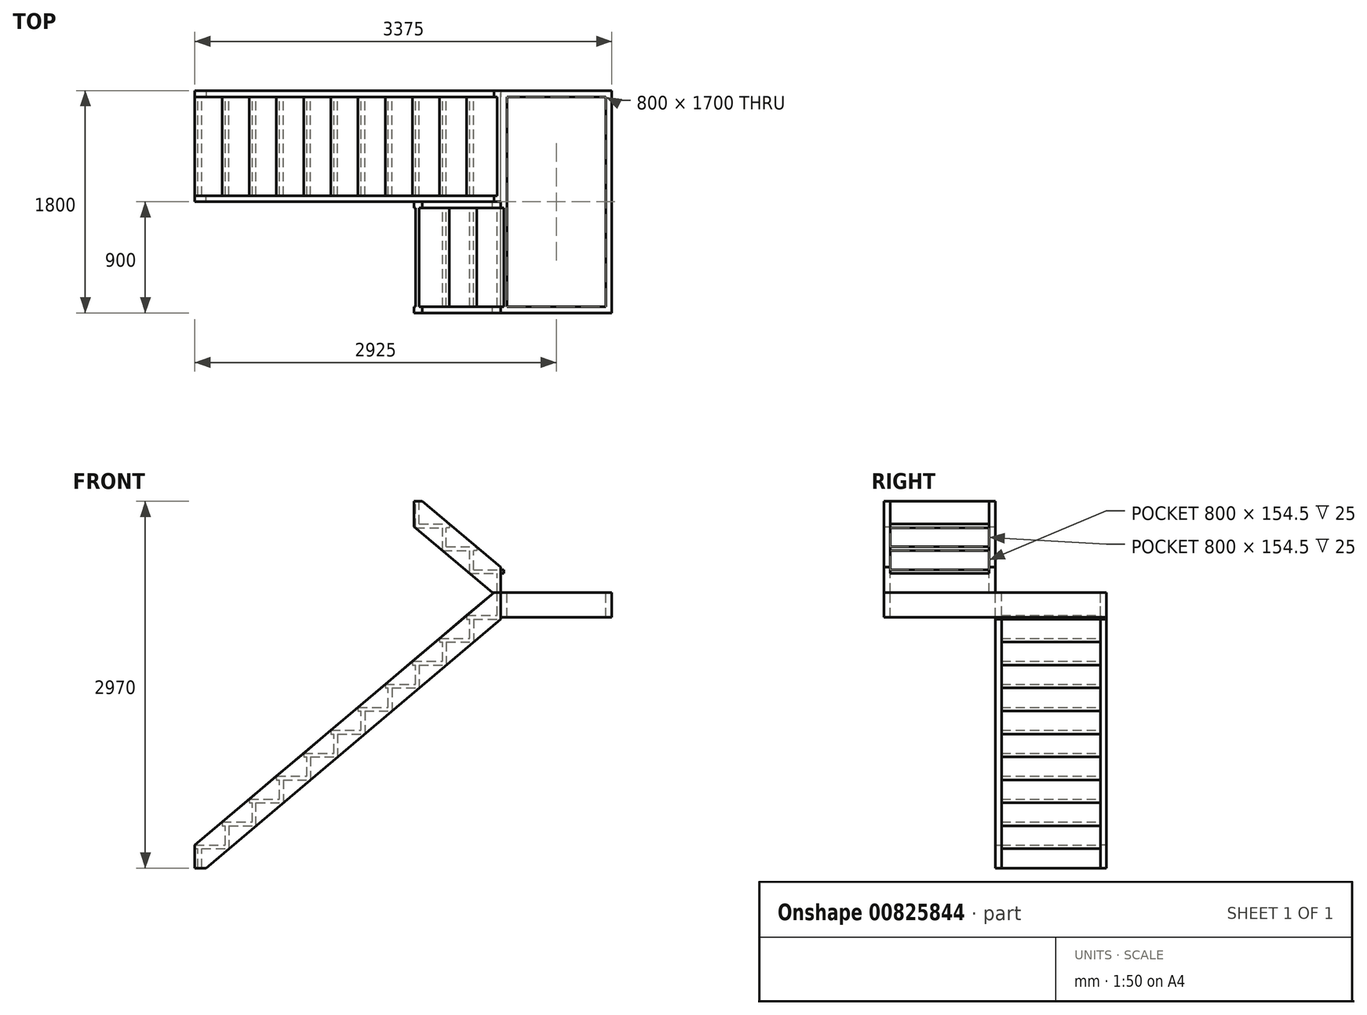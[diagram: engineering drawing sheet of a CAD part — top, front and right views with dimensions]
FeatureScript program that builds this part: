
annotation { "Feature Type Name" : "Feature", "Feature Type Description" : "" }
export const myFeature = defineFeature(function(context is Context, id is Id, definition is map)
    precondition{}
    {
        {
            var Q0;
            Q0=qCreatedBy(makeId("Front.planeOp"),FACE);
            var sketch = newSketch(context, id + "F0", { "sketchPlane" : qUnion([Q0])});
            skLineSegment(sketch, "E0", {"start": v(0, 0) * mm, "end": v(0, 156) * mm});
            skLineSegment(sketch, "E1", {"start": v(0, 186) * mm, "end": v(220, 186) * mm});
            skLineSegment(sketch, "E2", {"start": v(220, 186) * mm, "end": v(220, 342) * mm});
            skLineSegment(sketch, "E3", {"start": v(220, 372) * mm, "end": v(440, 372) * mm});
            skLineSegment(sketch, "E4", {"start": v(440, 372) * mm, "end": v(440, 528) * mm});
            skLineSegment(sketch, "E5", {"start": v(440, 558) * mm, "end": v(660, 558) * mm});
            skLineSegment(sketch, "E6", {"start": v(660, 558) * mm, "end": v(660, 714) * mm});
            skLineSegment(sketch, "E7", {"start": v(660, 744) * mm, "end": v(880, 744) * mm});
            skLineSegment(sketch, "E8", {"start": v(880, 744) * mm, "end": v(880, 900) * mm});
            skLineSegment(sketch, "E9", {"start": v(880, 930) * mm, "end": v(1100, 930) * mm});
            skLineSegment(sketch, "E10", {"start": v(1100, 930) * mm, "end": v(1100, 1086) * mm});
            skLineSegment(sketch, "E11", {"start": v(1100, 1116) * mm, "end": v(1320, 1116) * mm});
            skLineSegment(sketch, "E12", {"start": v(1320, 1116) * mm, "end": v(1320, 1272) * mm});
            skLineSegment(sketch, "E13", {"start": v(1320, 1302) * mm, "end": v(1540, 1302) * mm});
            skLineSegment(sketch, "E14", {"start": v(1540, 1302) * mm, "end": v(1540, 1458) * mm});
            skLineSegment(sketch, "E15", {"start": v(1540, 1488) * mm, "end": v(1760, 1488) * mm});
            skLineSegment(sketch, "E16", {"start": v(1760, 1488) * mm, "end": v(1760, 1644) * mm});
            skLineSegment(sketch, "E17", {"start": v(1760, 1674) * mm, "end": v(1980, 1674) * mm});
            skLineSegment(sketch, "E18", {"start": v(1980, 1674) * mm, "end": v(1980, 1830) * mm});
            skLineSegment(sketch, "E19", {"start": v(1980, 1860) * mm, "end": v(2200, 1860) * mm});
            skLineSegment(sketch, "E20", {"start": v(2200, 1860) * mm, "end": v(2200, 2016) * mm});
            skLineSegment(sketch, "E21", {"start": v(2200, 2046) * mm, "end": v(2420, 2046) * mm});
            skLineSegment(sketch, "E22", {"start": v(2420, 2046) * mm, "end": v(2420, 2232) * mm});
            skLineSegment(sketch, "E23.0", {"start": v(2230, 1860) * mm, "end": v(2230, 2016) * mm});
            skLineSegment(sketch, "E24.0", {"start": v(2200, 2016) * mm, "end": v(2420, 2016) * mm});
            skLineSegment(sketch, "E25.0", {"start": v(1980, 1830) * mm, "end": v(2200, 1830) * mm});
            skLineSegment(sketch, "E26.0", {"start": v(1760, 1644) * mm, "end": v(1980, 1644) * mm});
            skLineSegment(sketch, "E27.0", {"start": v(1790, 1488) * mm, "end": v(1790, 1644) * mm});
            skLineSegment(sketch, "E28.0", {"start": v(1540, 1458) * mm, "end": v(1760, 1458) * mm});
            skLineSegment(sketch, "E29.0", {"start": v(1570, 1302) * mm, "end": v(1570, 1458) * mm});
            skLineSegment(sketch, "E30.0", {"start": v(1320, 1272) * mm, "end": v(1540, 1272) * mm});
            skLineSegment(sketch, "E31.0", {"start": v(1350, 1116) * mm, "end": v(1350, 1272) * mm});
            skLineSegment(sketch, "E32.0", {"start": v(1100, 1086) * mm, "end": v(1320, 1086) * mm});
            skLineSegment(sketch, "E33.0", {"start": v(1130, 930) * mm, "end": v(1130, 1086) * mm});
            skLineSegment(sketch, "E34.0", {"start": v(880, 900) * mm, "end": v(1100, 900) * mm});
            skLineSegment(sketch, "E35.0", {"start": v(910, 744) * mm, "end": v(910, 900) * mm});
            skLineSegment(sketch, "E36.0", {"start": v(660, 714) * mm, "end": v(880, 714) * mm});
            skLineSegment(sketch, "E37.0", {"start": v(690, 558) * mm, "end": v(690, 714) * mm});
            skLineSegment(sketch, "E38.0", {"start": v(440, 528) * mm, "end": v(660, 528) * mm});
            skLineSegment(sketch, "E39.0", {"start": v(470, 372) * mm, "end": v(470, 528) * mm});
            skLineSegment(sketch, "E40.0", {"start": v(220, 342) * mm, "end": v(440, 342) * mm});
            skLineSegment(sketch, "E41.0", {"start": v(250, 186) * mm, "end": v(250, 342) * mm});
            skLineSegment(sketch, "E42.0", {"start": v(0, 156) * mm, "end": v(220, 156) * mm});
            skLineSegment(sketch, "E43.0", {"start": v(30, 0) * mm, "end": v(30, 156) * mm});
            skLineSegment(sketch, "E44", {"start": v(0, 0) * mm, "end": v(30, 0) * mm});
            skLineSegment(sketch, "E45", {"start": v(220, 156) * mm, "end": v(250, 156) * mm});
            skLineSegment(sketch, "E46", {"start": v(250, 186) * mm, "end": v(250, 156) * mm});
            skLineSegment(sketch, "E47", {"start": v(440, 342) * mm, "end": v(470, 342) * mm});
            skLineSegment(sketch, "E48", {"start": v(690, 558) * mm, "end": v(690, 528) * mm});
            skLineSegment(sketch, "E49", {"start": v(690, 528) * mm, "end": v(660, 528) * mm});
            skLineSegment(sketch, "E50", {"start": v(910, 744) * mm, "end": v(910, 714) * mm});
            skLineSegment(sketch, "E51", {"start": v(910, 714) * mm, "end": v(880, 714) * mm});
            skLineSegment(sketch, "E52", {"start": v(1130, 930) * mm, "end": v(1130, 900) * mm});
            skLineSegment(sketch, "E53", {"start": v(1130, 900) * mm, "end": v(1100, 900) * mm});
            skLineSegment(sketch, "E54", {"start": v(1350, 1116) * mm, "end": v(1350, 1086) * mm});
            skLineSegment(sketch, "E55", {"start": v(1350, 1086) * mm, "end": v(1320, 1086) * mm});
            skLineSegment(sketch, "E56", {"start": v(1570, 1302) * mm, "end": v(1570, 1272) * mm});
            skLineSegment(sketch, "E57", {"start": v(1570, 1272) * mm, "end": v(1540, 1272) * mm});
            skLineSegment(sketch, "E58", {"start": v(1790, 1488) * mm, "end": v(1790, 1458) * mm});
            skLineSegment(sketch, "E59", {"start": v(1790, 1458) * mm, "end": v(1760, 1458) * mm});
            skLineSegment(sketch, "E60", {"start": v(2010, 1674) * mm, "end": v(2010, 1644) * mm});
            skLineSegment(sketch, "E61", {"start": v(2010, 1644) * mm, "end": v(1980, 1644) * mm});
            skLineSegment(sketch, "E62", {"start": v(2230, 1860) * mm, "end": v(2230, 1830) * mm});
            skLineSegment(sketch, "E63", {"start": v(2230, 1830) * mm, "end": v(2200, 1830) * mm});
            skLineSegment(sketch, "E64", {"start": v(2200, 2046) * mm, "end": v(2175, 2046) * mm});
            skLineSegment(sketch, "E65", {"start": v(2175, 2046) * mm, "end": v(2175, 2016) * mm});
            skLineSegment(sketch, "E66", {"start": v(2175, 2016) * mm, "end": v(2200, 2016) * mm});
            skLineSegment(sketch, "E67", {"start": v(1980, 1860) * mm, "end": v(1955, 1860) * mm});
            skLineSegment(sketch, "E68", {"start": v(1955, 1860) * mm, "end": v(1955, 1830) * mm});
            skLineSegment(sketch, "E69", {"start": v(1955, 1830) * mm, "end": v(1980, 1830) * mm});
            skLineSegment(sketch, "E70", {"start": v(1760, 1674) * mm, "end": v(1735, 1674) * mm});
            skLineSegment(sketch, "E71", {"start": v(1735, 1674) * mm, "end": v(1735, 1644) * mm});
            skLineSegment(sketch, "E72", {"start": v(1735, 1644) * mm, "end": v(1760, 1644) * mm});
            skLineSegment(sketch, "E73", {"start": v(1540, 1488) * mm, "end": v(1515, 1488) * mm});
            skLineSegment(sketch, "E74", {"start": v(1515, 1488) * mm, "end": v(1515, 1458) * mm});
            skLineSegment(sketch, "E75", {"start": v(1515, 1458) * mm, "end": v(1540, 1458) * mm});
            skLineSegment(sketch, "E76", {"start": v(1320, 1302) * mm, "end": v(1295, 1302) * mm});
            skLineSegment(sketch, "E77", {"start": v(1295, 1302) * mm, "end": v(1295, 1272) * mm});
            skLineSegment(sketch, "E78", {"start": v(1295, 1272) * mm, "end": v(1320, 1272) * mm});
            skLineSegment(sketch, "E79", {"start": v(1100, 1116) * mm, "end": v(1075, 1116) * mm});
            skLineSegment(sketch, "E80", {"start": v(1075, 1116) * mm, "end": v(1075, 1086) * mm});
            skLineSegment(sketch, "E81", {"start": v(1075, 1086) * mm, "end": v(1100, 1086) * mm});
            skLineSegment(sketch, "E82", {"start": v(880, 930) * mm, "end": v(855, 930) * mm});
            skLineSegment(sketch, "E83", {"start": v(855, 930) * mm, "end": v(855, 900) * mm});
            skLineSegment(sketch, "E84", {"start": v(855, 900) * mm, "end": v(880, 900) * mm});
            skLineSegment(sketch, "E85", {"start": v(660, 744) * mm, "end": v(635, 744) * mm});
            skLineSegment(sketch, "E86", {"start": v(635, 744) * mm, "end": v(635, 714) * mm});
            skLineSegment(sketch, "E87", {"start": v(635, 714) * mm, "end": v(660, 714) * mm});
            skLineSegment(sketch, "E88", {"start": v(440, 558) * mm, "end": v(415, 558) * mm});
            skLineSegment(sketch, "E89", {"start": v(415, 558) * mm, "end": v(415, 528) * mm});
            skLineSegment(sketch, "E90", {"start": v(415, 528) * mm, "end": v(440, 528) * mm});
            skLineSegment(sketch, "E91", {"start": v(220, 372) * mm, "end": v(195, 372) * mm});
            skLineSegment(sketch, "E92", {"start": v(195, 372) * mm, "end": v(195, 342) * mm});
            skLineSegment(sketch, "E93", {"start": v(0, 186) * mm, "end": v(-25, 186) * mm});
            skLineSegment(sketch, "E94", {"start": v(-25, 186) * mm, "end": v(-25, 156) * mm});
            skLineSegment(sketch, "E95", {"start": v(-25, 156) * mm, "end": v(0, 156) * mm});
            skLineSegment(sketch, "E96", {"start": v(195, 342) * mm, "end": v(220, 342) * mm});
            skLineSegment(sketch, "E97", {"start": v(470, 342) * mm, "end": v(470, 372) * mm});
            skLineSegment(sketch, "E98", {"start": v(2010, 1674) * mm, "end": v(2010, 1830) * mm});
            skLineSegment(sketch, "E99.0", {"start": v(2450, 2016) * mm, "end": v(2450, 2232) * mm});
            skLineSegment(sketch, "E100", {"start": v(2420, 2016) * mm, "end": v(2450, 2016) * mm});
            skLineSegment(sketch, "E101", {"start": v(2420, 2232) * mm, "end": v(2450, 2232) * mm});
            skLineSegment(sketch, "E102", {"start": v(2420, 2046) * mm, "end": v(2450, 2046) * mm});
            skLineSegment(sketch, "E103", {"start": v(2200, 1860) * mm, "end": v(2230, 1860) * mm});
            skLineSegment(sketch, "E104", {"start": v(1980, 1674) * mm, "end": v(2010, 1674) * mm});
            skLineSegment(sketch, "E105", {"start": v(1760, 1488) * mm, "end": v(1790, 1488) * mm});
            skLineSegment(sketch, "E106", {"start": v(1540, 1302) * mm, "end": v(1570, 1302) * mm});
            skLineSegment(sketch, "E107", {"start": v(1320, 1116) * mm, "end": v(1350, 1116) * mm});
            skLineSegment(sketch, "E108", {"start": v(1100, 930) * mm, "end": v(1130, 930) * mm});
            skLineSegment(sketch, "E109", {"start": v(880, 744) * mm, "end": v(910, 744) * mm});
            skLineSegment(sketch, "E110", {"start": v(660, 558) * mm, "end": v(690, 558) * mm});
            skLineSegment(sketch, "E111", {"start": v(440, 372) * mm, "end": v(470, 372) * mm});
            skLineSegment(sketch, "E112", {"start": v(220, 186) * mm, "end": v(250, 186) * mm});
            skSolve(sketch);
        }
        {
            var Q0;
            Q0=qCreatedBy(makeId("Front.planeOp"),FACE);
            var sketch = newSketch(context, id + "F1", { "sketchPlane" : qUnion([Q0])});
            skLineSegment(sketch, "E113", {"start": v(2420, 2232) * mm, "end": v(2420, 2416.5) * mm});
            skLineSegment(sketch, "E114", {"start": v(2420, 2416.5) * mm, "end": v(2200, 2416.5) * mm});
            skLineSegment(sketch, "E115", {"start": v(2200, 2416.5) * mm, "end": v(2200, 2601) * mm});
            skLineSegment(sketch, "E116", {"start": v(2200, 2601) * mm, "end": v(1980, 2601) * mm});
            skLineSegment(sketch, "E117", {"start": v(1980, 2601) * mm, "end": v(1980, 2785.5) * mm});
            skLineSegment(sketch, "E118", {"start": v(1980, 2785.5) * mm, "end": v(1760, 2785.5) * mm});
            skLineSegment(sketch, "E119", {"start": v(1760, 2785.5) * mm, "end": v(1760, 2970) * mm});
            skPoint(sketch, "E120.end.orphan", {"position": v(1760, 2970) * mm});
            skSolve(sketch);
        }
        {
            var Q0;
            Q0=qCreatedBy(makeId("Front.planeOp"),FACE);
            var sketch = newSketch(context, id + "F2", { "sketchPlane" : qUnion([Q0])});
            skLineSegment(sketch, "E121", {"start": v(0, 0) * mm, "end": v(4057.25, 0) * mm, "construction": true});
            skLineSegment(sketch, "E122.0", {"start": v(0, 2775) * mm, "end": v(4057.25, 2775) * mm, "construction": true});
            skLineSegment(sketch, "E123.0", {"start": v(0, 775) * mm, "end": v(4057.25, 775) * mm, "construction": true});
            skLineSegment(sketch, "E124", {"start": v(660, 714) * mm, "end": v(660, 3042.77) * mm, "construction": true});
            skSolve(sketch);
        }
        {
            var Q0;
            Q0 = qSketchRegion(id + "F0", true);
            extrude(context, id + "F3", {"entities" : qUnion([Q0]), "depth" : 800 * mm, "offsetDistance" : 25 * mm});
        }
        {
            var Q0;
            Q0=qCreatedBy(makeId("Front.planeOp"),FACE);
            var sketch = newSketch(context, id + "F4", { "sketchPlane" : qUnion([Q0])});
            skLineSegment(sketch, "E125", {"start": v(-25, 186) * mm, "end": v(2395, 2232) * mm});
            skLineSegment(sketch, "E126", {"start": v(65.48, 0) * mm, "end": v(2450, 2016) * mm});
            skLineSegment(sketch, "E127", {"start": v(2395, 2232) * mm, "end": v(2450, 2232) * mm});
            skLineSegment(sketch, "E128", {"start": v(2450, 2232) * mm, "end": v(2450, 2016) * mm});
            skLineSegment(sketch, "E129", {"start": v(-25, 186) * mm, "end": v(-25, 0) * mm});
            skLineSegment(sketch, "E130", {"start": v(-25, 0) * mm, "end": v(65.48, 0) * mm});
            skSolve(sketch);
        }
        {
            var Q0;
            Q0 = qSketchRegion(id + "F0", true);
            extrude(context, id + "F5", {"entities" : qUnion([Q0]), "operationType" : NewBodyOperationType.ADD, "depth" : 800 * mm, "offsetDistance" : 25 * mm});
        }
        {
            var Q0;
            Q0 = qSketchRegion(id + "F4", true);
            extrude(context, id + "F6", {"entities" : qUnion([Q0]), "operationType" : NewBodyOperationType.ADD, "oppositeDirection" : true, "depth" : 50 * mm, "offsetDistance" : 25 * mm});
        }
        {
            var Q0;
            Q0=makeQuery(id+"F3.opExtrude","CAP_FACE",FACE,{"disambiguationData":[OSD([sQuery(id+"F0.wireOp",EDGE,"E0"),sQuery(id+"F0.wireOp",EDGE,"E1"),sQuery(id+"F0.wireOp",EDGE,"E2"),sQuery(id+"F0.wireOp",EDGE,"E3"),sQuery(id+"F0.wireOp",EDGE,"E4"),sQuery(id+"F0.wireOp",EDGE,"E5"),sQuery(id+"F0.wireOp",EDGE,"E6"),sQuery(id+"F0.wireOp",EDGE,"E7"),sQuery(id+"F0.wireOp",EDGE,"E8"),sQuery(id+"F0.wireOp",EDGE,"E9"),sQuery(id+"F0.wireOp",EDGE,"E10"),sQuery(id+"F0.wireOp",EDGE,"E11"),sQuery(id+"F0.wireOp",EDGE,"E12"),sQuery(id+"F0.wireOp",EDGE,"E13"),sQuery(id+"F0.wireOp",EDGE,"E14"),sQuery(id+"F0.wireOp",EDGE,"E15"),sQuery(id+"F0.wireOp",EDGE,"E16"),sQuery(id+"F0.wireOp",EDGE,"E17"),sQuery(id+"F0.wireOp",EDGE,"E18"),sQuery(id+"F0.wireOp",EDGE,"E19"),sQuery(id+"F0.wireOp",EDGE,"E20"),sQuery(id+"F0.wireOp",EDGE,"E21"),sQuery(id+"F0.wireOp",EDGE,"E22"),sQuery(id+"F0.wireOp",EDGE,"E23.0"),sQuery(id+"F0.wireOp",EDGE,"E24.0"),sQuery(id+"F0.wireOp",EDGE,"E25.0"),sQuery(id+"F0.wireOp",EDGE,"E26.0"),sQuery(id+"F0.wireOp",EDGE,"E27.0"),sQuery(id+"F0.wireOp",EDGE,"E28.0"),sQuery(id+"F0.wireOp",EDGE,"E29.0"),sQuery(id+"F0.wireOp",EDGE,"E30.0"),sQuery(id+"F0.wireOp",EDGE,"E31.0"),sQuery(id+"F0.wireOp",EDGE,"E32.0"),sQuery(id+"F0.wireOp",EDGE,"E33.0"),sQuery(id+"F0.wireOp",EDGE,"E34.0"),sQuery(id+"F0.wireOp",EDGE,"E35.0"),sQuery(id+"F0.wireOp",EDGE,"E36.0"),sQuery(id+"F0.wireOp",EDGE,"E37.0"),sQuery(id+"F0.wireOp",EDGE,"E38.0"),sQuery(id+"F0.wireOp",EDGE,"E39.0"),sQuery(id+"F0.wireOp",EDGE,"E40.0"),sQuery(id+"F0.wireOp",EDGE,"E41.0"),sQuery(id+"F0.wireOp",EDGE,"E42.0"),sQuery(id+"F0.wireOp",EDGE,"E43.0"),sQuery(id+"F0.wireOp",EDGE,"E44"),sQuery(id+"F0.wireOp",EDGE,"E45"),sQuery(id+"F0.wireOp",EDGE,"E46"),sQuery(id+"F0.wireOp",EDGE,"E47"),sQuery(id+"F0.wireOp",EDGE,"E48"),sQuery(id+"F0.wireOp",EDGE,"E49"),sQuery(id+"F0.wireOp",EDGE,"E50"),sQuery(id+"F0.wireOp",EDGE,"E51"),sQuery(id+"F0.wireOp",EDGE,"E52"),sQuery(id+"F0.wireOp",EDGE,"E53"),sQuery(id+"F0.wireOp",EDGE,"E54"),sQuery(id+"F0.wireOp",EDGE,"E55"),sQuery(id+"F0.wireOp",EDGE,"E56"),sQuery(id+"F0.wireOp",EDGE,"E57"),sQuery(id+"F0.wireOp",EDGE,"E58"),sQuery(id+"F0.wireOp",EDGE,"E59"),sQuery(id+"F0.wireOp",EDGE,"E60"),sQuery(id+"F0.wireOp",EDGE,"E61"),sQuery(id+"F0.wireOp",EDGE,"E62"),sQuery(id+"F0.wireOp",EDGE,"E63"),sQuery(id+"F0.wireOp",EDGE,"E64"),sQuery(id+"F0.wireOp",EDGE,"E65"),sQuery(id+"F0.wireOp",EDGE,"E66"),sQuery(id+"F0.wireOp",EDGE,"E67"),sQuery(id+"F0.wireOp",EDGE,"E68"),sQuery(id+"F0.wireOp",EDGE,"E69"),sQuery(id+"F0.wireOp",EDGE,"E70"),sQuery(id+"F0.wireOp",EDGE,"E71"),sQuery(id+"F0.wireOp",EDGE,"E72"),sQuery(id+"F0.wireOp",EDGE,"E73"),sQuery(id+"F0.wireOp",EDGE,"E74"),sQuery(id+"F0.wireOp",EDGE,"E75"),sQuery(id+"F0.wireOp",EDGE,"E76"),sQuery(id+"F0.wireOp",EDGE,"E77"),sQuery(id+"F0.wireOp",EDGE,"E78"),sQuery(id+"F0.wireOp",EDGE,"E79"),sQuery(id+"F0.wireOp",EDGE,"E80"),sQuery(id+"F0.wireOp",EDGE,"E81"),sQuery(id+"F0.wireOp",EDGE,"E82"),sQuery(id+"F0.wireOp",EDGE,"E83"),sQuery(id+"F0.wireOp",EDGE,"E84"),sQuery(id+"F0.wireOp",EDGE,"E85"),sQuery(id+"F0.wireOp",EDGE,"E86"),sQuery(id+"F0.wireOp",EDGE,"E87"),sQuery(id+"F0.wireOp",EDGE,"E88"),sQuery(id+"F0.wireOp",EDGE,"E89"),sQuery(id+"F0.wireOp",EDGE,"E90"),sQuery(id+"F0.wireOp",EDGE,"E91"),sQuery(id+"F0.wireOp",EDGE,"E92"),sQuery(id+"F0.wireOp",EDGE,"E93"),sQuery(id+"F0.wireOp",EDGE,"E94"),sQuery(id+"F0.wireOp",EDGE,"E95"),sQuery(id+"F0.wireOp",EDGE,"E96"),sQuery(id+"F0.wireOp",EDGE,"E97"),sQuery(id+"F0.wireOp",EDGE,"E98"),sQuery(id+"F0.wireOp",EDGE,"E99.0"),sQuery(id+"F0.wireOp",EDGE,"E100"),sQuery(id+"F0.wireOp",EDGE,"E101")])],"isStart":false});
            var sketch = newSketch(context, id + "F7", { "sketchPlane" : qUnion([Q0])});
            skLineSegment(sketch, "E131", {"start": v(2450, 2016) * mm, "end": v(2450, 2232) * mm});
            skLineSegment(sketch, "E132", {"start": v(2450, 2232) * mm, "end": v(2396.45, 2232) * mm});
            skLineSegment(sketch, "E133", {"start": v(2396.45, 2232) * mm, "end": v(-25, 186) * mm});
            skLineSegment(sketch, "E134", {"start": v(-25, 186) * mm, "end": v(-25, 0) * mm});
            skLineSegment(sketch, "E135", {"start": v(-25, 0) * mm, "end": v(65.48, 0) * mm});
            skLineSegment(sketch, "E136", {"start": v(65.48, 0) * mm, "end": v(2450, 2016) * mm});
            skSolve(sketch);
        }
        {
            var Q0;
            Q0 = qSketchRegion(id + "F7", true);
            extrude(context, id + "F8", {"entities" : qUnion([Q0]), "operationType" : NewBodyOperationType.ADD, "depth" : 50 * mm, "offsetDistance" : 25 * mm});
        }
        {
            var Q0;
            Q0=makeQuery(id+"F8.boolean.opBoolean","MERGE",FACE,{"derivedFrom":[makeQuery(id+"F6.boolean.opBoolean","MERGE",FACE,{"derivedFrom":[makeQuery(id+"F3.opExtrude","SWEPT_FACE",FACE,{"disambiguationData":[OSD([sQuery(id+"F0.wireOp",EDGE,"E101")])]}),makeQuery(id+"F6.opExtrude","SWEPT_FACE",FACE,{"disambiguationData":[OSD([sQuery(id+"F4.wireOp",EDGE,"E127")])]})]}),makeQuery(id+"F8.opExtrude","SWEPT_FACE",FACE,{"disambiguationData":[OSD([sQuery(id+"F7.wireOp",EDGE,"E132")])]})]});
            var sketch = newSketch(context, id + "F9", { "sketchPlane" : qUnion([Q0])});
            skLineSegment(sketch, "E137", {"start": v(2450, 50) * mm, "end": v(2450, -1750) * mm});
            skLineSegment(sketch, "E138", {"start": v(2450, -1750) * mm, "end": v(3350, -1750) * mm});
            skLineSegment(sketch, "E139", {"start": v(3350, -1750) * mm, "end": v(3350, 50) * mm});
            skLineSegment(sketch, "E140", {"start": v(3350, 50) * mm, "end": v(2450, 50) * mm});
            skLineSegment(sketch, "E141.0", {"start": v(3300, -1700) * mm, "end": v(3300, 0) * mm});
            skLineSegment(sketch, "E142.0", {"start": v(3300, 0) * mm, "end": v(2500, 0) * mm});
            skLineSegment(sketch, "E143.0", {"start": v(2500, 0) * mm, "end": v(2500, -1700) * mm});
            skLineSegment(sketch, "E144.0", {"start": v(2500, -1700) * mm, "end": v(3300, -1700) * mm});
            skSolve(sketch);
        }
        {
            var Q0;
            Q0 = qSketchRegion(id + "F9", true);
            extrude(context, id + "F10", {"entities" : qUnion([Q0]), "operationType" : NewBodyOperationType.ADD, "oppositeDirection" : true, "depth" : 200 * mm, "offsetDistance" : 25 * mm});
        }
        {
            var Q0;
            Q0=makeQuery(id+"F8.opExtrude","CAP_FACE",FACE,{"disambiguationData":[OSD([sQuery(id+"F7.wireOp",EDGE,"E131"),sQuery(id+"F7.wireOp",EDGE,"E132"),sQuery(id+"F7.wireOp",EDGE,"E133"),sQuery(id+"F7.wireOp",EDGE,"E134"),sQuery(id+"F7.wireOp",EDGE,"E135"),sQuery(id+"F7.wireOp",EDGE,"E136")])],"isStart":false});
            var sketch = newSketch(context, id + "F11", { "sketchPlane" : qUnion([Q0])});
            skLineSegment(sketch, "E145", {"start": v(2450, 2232) * mm, "end": v(2450, 2416.5) * mm, "construction": true});
            skLineSegment(sketch, "E146", {"start": v(2450, 2416.5) * mm, "end": v(2230, 2416.5) * mm, "construction": true});
            skLineSegment(sketch, "E147", {"start": v(2230, 2416.5) * mm, "end": v(2230, 2601) * mm, "construction": true});
            skLineSegment(sketch, "E148", {"start": v(2230, 2601) * mm, "end": v(2010, 2601) * mm, "construction": true});
            skLineSegment(sketch, "E149", {"start": v(2010, 2601) * mm, "end": v(2010, 2785.5) * mm, "construction": true});
            skLineSegment(sketch, "E150", {"start": v(2010, 2785.5) * mm, "end": v(1790, 2785.5) * mm, "construction": true});
            skLineSegment(sketch, "E151", {"start": v(1790, 2785.5) * mm, "end": v(1790, 2970) * mm, "construction": true});
            skLineSegment(sketch, "E152.0", {"start": v(1760, 2970) * mm, "end": v(1760, 2971.67) * mm, "construction": true});
            skLineSegment(sketch, "E153.0", {"start": v(2010, 2755.5) * mm, "end": v(1790, 2755.5) * mm, "construction": true});
            skLineSegment(sketch, "E154.0", {"start": v(1980, 2601) * mm, "end": v(1980, 2785.5) * mm, "construction": true});
            skLineSegment(sketch, "E155.0", {"start": v(2230, 2571) * mm, "end": v(2010, 2571) * mm, "construction": true});
            skLineSegment(sketch, "E156.0", {"start": v(2200, 2416.5) * mm, "end": v(2200, 2601) * mm, "construction": true});
            skLineSegment(sketch, "E157.0", {"start": v(2450, 2386.5) * mm, "end": v(2230, 2386.5) * mm, "construction": true});
            skLineSegment(sketch, "E158", {"start": v(2200, 2416.5) * mm, "end": v(2200, 2386.5) * mm, "construction": true});
            skLineSegment(sketch, "E159", {"start": v(2200, 2386.5) * mm, "end": v(2230, 2386.5) * mm, "construction": true});
            skLineSegment(sketch, "E160", {"start": v(2010, 2571) * mm, "end": v(1980, 2571) * mm, "construction": true});
            skLineSegment(sketch, "E161", {"start": v(1980, 2571) * mm, "end": v(1980, 2601) * mm, "construction": true});
            skLineSegment(sketch, "E162", {"start": v(1790, 2755.5) * mm, "end": v(1760, 2755.5) * mm, "construction": true});
            skLineSegment(sketch, "E163.0", {"start": v(2420, 2232) * mm, "end": v(2420, 2416.5) * mm});
            skLineSegment(sketch, "E164", {"start": v(2450, 2232) * mm, "end": v(2450, 2416.5) * mm});
            skLineSegment(sketch, "E165", {"start": v(1760, 2971.67) * mm, "end": v(1760, 2970) * mm});
            skLineSegment(sketch, "E166.0", {"start": v(2170, 2416.5) * mm, "end": v(2170, 2386.5) * mm});
            skLineSegment(sketch, "E167.0", {"start": v(1749.23, 2764.53) * mm, "end": v(1749.23, 2794.53) * mm, "construction": true});
            skLineSegment(sketch, "E168.0", {"start": v(1730, 2785.5) * mm, "end": v(1730, 2970) * mm, "construction": true});
            skLineSegment(sketch, "E169", {"start": v(1790, 2970) * mm, "end": v(1730, 2970) * mm});
            skLineSegment(sketch, "E170", {"start": v(1749.23, 2970.9) * mm, "end": v(1749.23, 2764.53) * mm});
            skLineSegment(sketch, "E171", {"start": v(1749.23, 2764.53) * mm, "end": v(2384.23, 2232) * mm});
            skLineSegment(sketch, "E172", {"start": v(2450, 2232) * mm, "end": v(2384.23, 2232) * mm});
            skPoint(sketch, "E173.orphan", {"position": v(2384.23, 2232) * mm});
            skLineSegment(sketch, "E174.trimOffspring", {"start": v(2170, 2411.66) * mm, "end": v(2200, 2386.5) * mm});
            skPoint(sketch, "E175.end.orphan", {"position": v(1760, 2785.5) * mm});
            skLineSegment(sketch, "E176", {"start": v(2450, 2386.5) * mm, "end": v(2475, 2386.5) * mm, "construction": true});
            skLineSegment(sketch, "E177", {"start": v(2475, 2386.5) * mm, "end": v(2475, 2416.5) * mm, "construction": true});
            skLineSegment(sketch, "E178", {"start": v(2475, 2416.5) * mm, "end": v(2450, 2416.5) * mm, "construction": true});
            skLineSegment(sketch, "E179", {"start": v(2230, 2601) * mm, "end": v(2255, 2601) * mm});
            skLineSegment(sketch, "E180", {"start": v(2255, 2601) * mm, "end": v(2255, 2571) * mm});
            skLineSegment(sketch, "E181", {"start": v(2255, 2571) * mm, "end": v(2230, 2571) * mm});
            skLineSegment(sketch, "E182", {"start": v(2010, 2785.5) * mm, "end": v(2035, 2785.5) * mm});
            skLineSegment(sketch, "E183", {"start": v(2035, 2785.5) * mm, "end": v(2035, 2755.5) * mm});
            skLineSegment(sketch, "E184", {"start": v(2035, 2755.5) * mm, "end": v(2010, 2755.5) * mm});
            skLineSegment(sketch, "E185", {"start": v(2450, 2416.5) * mm, "end": v(2450, 2437.47) * mm});
            skLineSegment(sketch, "E186", {"start": v(2450, 2437.47) * mm, "end": v(1815, 2970) * mm});
            skLineSegment(sketch, "E187", {"start": v(1815, 2970) * mm, "end": v(1790, 2970) * mm});
            skSolve(sketch);
        }
        {
            var Q0;
            Q0 = qSketchRegion(id + "F11", true);
            extrude(context, id + "F12", {"entities" : qUnion([Q0]), "depth" : 50 * mm, "offsetDistance" : 25 * mm});
        }
        {
            var Q0;
            Q0=makeQuery(id+"F12.opExtrude","CAP_FACE",FACE,{"disambiguationData":[OSD([sQuery(id+"F11.wireOp",EDGE,"E164"),sQuery(id+"F11.wireOp",EDGE,"1kJficIn-a1Za-3pRF-JXdC-2xlpCL5zuOAs"),sQuery(id+"F11.wireOp",EDGE,"E165"),sQuery(id+"F11.wireOp",EDGE,"MYEBM5Jr-QzQh-At56-vD5c-EMdVx3Uxf2dO"),sQuery(id+"F11.wireOp",EDGE,"czr8V54X-4PEG-ZS08-VHQo-Zryb2TXv87s3"),sQuery(id+"F11.wireOp",EDGE,"EJKhbDLx-IS0X-3xD9-N9LD-pQFudp6GmxO2")])],"isStart":false});
            var sketch = newSketch(context, id + "F13", { "sketchPlane" : qUnion([Q0])});
            skLineSegment(sketch, "E188", {"start": v(2450, 2232) * mm, "end": v(2450, 2386.5) * mm});
            skLineSegment(sketch, "E189", {"start": v(2450, 2416.5) * mm, "end": v(2230, 2416.5) * mm});
            skLineSegment(sketch, "E190", {"start": v(2230, 2416.5) * mm, "end": v(2230, 2571) * mm});
            skLineSegment(sketch, "E191", {"start": v(2230, 2601) * mm, "end": v(2010, 2601) * mm});
            skLineSegment(sketch, "E192", {"start": v(2010, 2601) * mm, "end": v(2010, 2755.5) * mm});
            skLineSegment(sketch, "E193", {"start": v(2010, 2785.5) * mm, "end": v(1790, 2785.5) * mm});
            skLineSegment(sketch, "E194", {"start": v(1790, 2785.5) * mm, "end": v(1790, 2970) * mm});
            skLineSegment(sketch, "E195.0", {"start": v(1760, 2785.5) * mm, "end": v(1760, 2970) * mm});
            skLineSegment(sketch, "E196.0", {"start": v(1980, 2601) * mm, "end": v(1980, 2755.5) * mm});
            skLineSegment(sketch, "E197.0", {"start": v(2200, 2416.5) * mm, "end": v(2200, 2571) * mm});
            skLineSegment(sketch, "E198.0", {"start": v(2420, 2232) * mm, "end": v(2420, 2386.5) * mm});
            skLineSegment(sketch, "E199.0", {"start": v(2450, 2386.5) * mm, "end": v(2230, 2386.5) * mm});
            skLineSegment(sketch, "E200.0", {"start": v(2230, 2571) * mm, "end": v(2010, 2571) * mm});
            skLineSegment(sketch, "E201.0", {"start": v(2010, 2755.5) * mm, "end": v(1790, 2755.5) * mm});
            skLineSegment(sketch, "E202", {"start": v(1760, 2785.5) * mm, "end": v(1760, 2755.5) * mm});
            skLineSegment(sketch, "E203", {"start": v(1760, 2755.5) * mm, "end": v(1790, 2755.5) * mm});
            skLineSegment(sketch, "E204", {"start": v(1980, 2601) * mm, "end": v(1980, 2571) * mm});
            skLineSegment(sketch, "E205", {"start": v(1980, 2571) * mm, "end": v(2010, 2571) * mm});
            skLineSegment(sketch, "E206", {"start": v(2200, 2416.5) * mm, "end": v(2200, 2386.5) * mm});
            skLineSegment(sketch, "E207", {"start": v(2200, 2386.5) * mm, "end": v(2230, 2386.5) * mm});
            skLineSegment(sketch, "E208", {"start": v(2420, 2232) * mm, "end": v(2450, 2232) * mm});
            skLineSegment(sketch, "E209", {"start": v(2450, 2416.5) * mm, "end": v(2475, 2416.5) * mm});
            skLineSegment(sketch, "E210", {"start": v(2475, 2416.5) * mm, "end": v(2475, 2386.5) * mm});
            skLineSegment(sketch, "E211", {"start": v(2475, 2386.5) * mm, "end": v(2450, 2386.5) * mm});
            skLineSegment(sketch, "E212", {"start": v(2230, 2601) * mm, "end": v(2255, 2601) * mm});
            skLineSegment(sketch, "E213", {"start": v(2255, 2601) * mm, "end": v(2255, 2571) * mm});
            skLineSegment(sketch, "E214", {"start": v(2255, 2571) * mm, "end": v(2230, 2571) * mm});
            skLineSegment(sketch, "E215", {"start": v(2010, 2785.5) * mm, "end": v(2035, 2785.5) * mm});
            skLineSegment(sketch, "E216", {"start": v(2035, 2785.5) * mm, "end": v(2035, 2755.5) * mm});
            skLineSegment(sketch, "E217", {"start": v(2035, 2755.5) * mm, "end": v(2010, 2755.5) * mm});
            skLineSegment(sketch, "E218", {"start": v(1790, 2785.5) * mm, "end": v(1760, 2785.5) * mm});
            skLineSegment(sketch, "E219", {"start": v(2010, 2601) * mm, "end": v(1980, 2601) * mm});
            skLineSegment(sketch, "E220", {"start": v(2230, 2416.5) * mm, "end": v(2200, 2416.5) * mm});
            skLineSegment(sketch, "E221", {"start": v(1760, 2970) * mm, "end": v(1790, 2970) * mm});
            skSolve(sketch);
        }
        {
            var Q0;
            Q0 = qSketchRegion(id + "F13", true);
            extrude(context, id + "F14", {"entities" : qUnion([Q0]), "operationType" : NewBodyOperationType.ADD, "depth" : 800 * mm, "offsetDistance" : 25 * mm});
        }
        {
            var Q0;
            Q0=makeQuery(id+"F14.opExtrude","CAP_FACE",FACE,{"disambiguationData":[OSD([sQuery(id+"F13.wireOp",EDGE,"E188"),sQuery(id+"F13.wireOp",EDGE,"E189"),sQuery(id+"F13.wireOp",EDGE,"E190"),sQuery(id+"F13.wireOp",EDGE,"E191"),sQuery(id+"F13.wireOp",EDGE,"E192"),sQuery(id+"F13.wireOp",EDGE,"E193"),sQuery(id+"F13.wireOp",EDGE,"E194"),sQuery(id+"F13.wireOp",EDGE,"E195.0"),sQuery(id+"F13.wireOp",EDGE,"E196.0"),sQuery(id+"F13.wireOp",EDGE,"E197.0"),sQuery(id+"F13.wireOp",EDGE,"E198.0"),sQuery(id+"F13.wireOp",EDGE,"E199.0"),sQuery(id+"F13.wireOp",EDGE,"E200.0"),sQuery(id+"F13.wireOp",EDGE,"E201.0"),sQuery(id+"F13.wireOp",EDGE,"E202"),sQuery(id+"F13.wireOp",EDGE,"E203"),sQuery(id+"F13.wireOp",EDGE,"E204"),sQuery(id+"F13.wireOp",EDGE,"E205"),sQuery(id+"F13.wireOp",EDGE,"E206"),sQuery(id+"F13.wireOp",EDGE,"E207"),sQuery(id+"F13.wireOp",EDGE,"E208"),sQuery(id+"F13.wireOp",EDGE,"E209"),sQuery(id+"F13.wireOp",EDGE,"E210"),sQuery(id+"F13.wireOp",EDGE,"E211"),sQuery(id+"F13.wireOp",EDGE,"E212"),sQuery(id+"F13.wireOp",EDGE,"E213"),sQuery(id+"F13.wireOp",EDGE,"E214"),sQuery(id+"F13.wireOp",EDGE,"E215"),sQuery(id+"F13.wireOp",EDGE,"E216"),sQuery(id+"F13.wireOp",EDGE,"E217"),sQuery(id+"F13.wireOp",EDGE,"E221")])],"isStart":false});
            var sketch = newSketch(context, id + "F15", { "sketchPlane" : qUnion([Q0])});
            skLineSegment(sketch, "E222", {"start": v(2450, 2232) * mm, "end": v(2450, 2437.47) * mm});
            skLineSegment(sketch, "E223", {"start": v(2450, 2437.47) * mm, "end": v(1815, 2970) * mm});
            skLineSegment(sketch, "E224", {"start": v(1815, 2970) * mm, "end": v(1749.23, 2970) * mm});
            skLineSegment(sketch, "E225", {"start": v(1749.23, 2970) * mm, "end": v(1749.23, 2764.53) * mm});
            skLineSegment(sketch, "E226", {"start": v(1749.23, 2764.53) * mm, "end": v(2384.23, 2232) * mm});
            skLineSegment(sketch, "E227", {"start": v(2384.23, 2232) * mm, "end": v(2450, 2232) * mm});
            skSolve(sketch);
        }
        {
            var Q0;
            Q0 = qSketchRegion(id + "F15", true);
            extrude(context, id + "F16", {"entities" : qUnion([Q0]), "operationType" : NewBodyOperationType.ADD, "depth" : 50 * mm, "offsetDistance" : 25 * mm});
        }
    });
